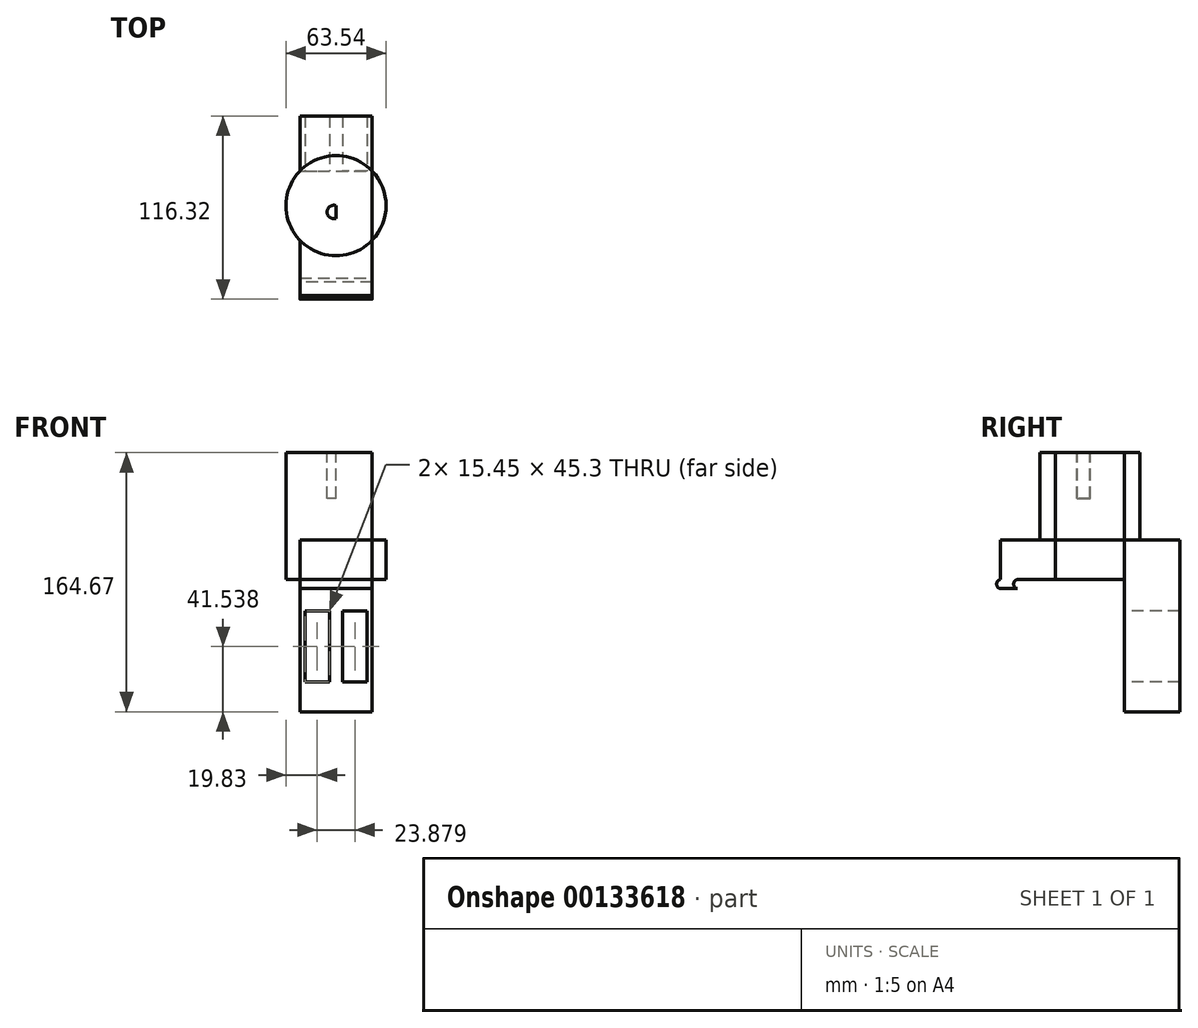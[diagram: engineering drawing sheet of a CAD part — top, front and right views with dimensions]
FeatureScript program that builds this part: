
annotation { "Feature Type Name" : "Feature", "Feature Type Description" : "" }
export const myFeature = defineFeature(function(context is Context, id is Id, definition is map)
    precondition{}
    {
        {
            var Q0;
            Q0=qCreatedBy(makeId("Top.planeOp"),FACE);
            var sketch = newSketch(context, id + "F0", { "sketchPlane" : qUnion([Q0])});
            skCircle(sketch, "E0", {"center": v(0, 0) * mm, "radius": 31.77 * mm});
            skLineSegment(sketch, "E1.bottom", {"start": v(22.97, -56.95) * mm, "end": v(-22.97, -56.95) * mm});
            skLineSegment(sketch, "E1.top", {"start": v(22.97, 56.95) * mm, "end": v(-22.97, 56.95) * mm});
            skLineSegment(sketch, "E1.left", {"start": v(22.97, -56.95) * mm, "end": v(22.97, 56.95) * mm});
            skLineSegment(sketch, "E1.right", {"start": v(-22.97, -56.95) * mm, "end": v(-22.97, 56.95) * mm});
            skSolve(sketch);
        }
        {
            var Q0;
            {var subQ0=sQuery(id+"F0.wireOp",EDGE,"E1.left");var subQ1=sQuery(id+"F0.wireOp",EDGE,"E0");var subQ2=makeQuery(id+"F0.imprint","INTERSECT",VERTEX,{"disambiguationData":[OD(0.0)],"derivedFrom":[subQ1,subQ0]});Q0=makeQuery(id+"F0.imprint","IMPRINT",FACE,{"disambiguationData":[TD([[makeQuery(id+"F0.imprint","IMPRINT",EDGE,{"disambiguationData":[TD([[subQ2,1.0]])],"derivedFrom":subQ1}),1.0]])]});}
            var Q1;
            {var subQ0=sQuery(id+"F0.wireOp",EDGE,"E1.right");var subQ1=sQuery(id+"F0.wireOp",EDGE,"E0");var subQ2=makeQuery(id+"F0.imprint","INTERSECT",VERTEX,{"disambiguationData":[OD(0.0)],"derivedFrom":[subQ1,subQ0]});Q1=makeQuery(id+"F0.imprint","IMPRINT",FACE,{"disambiguationData":[TD([[makeQuery(id+"F0.imprint","IMPRINT",EDGE,{"disambiguationData":[TD([[subQ2,1.0]])],"derivedFrom":subQ1}),1.0]])]});}
            var Q2;
            {var subQ0=sQuery(id+"F0.wireOp",EDGE,"E1.right");var subQ1=sQuery(id+"F0.wireOp",EDGE,"E0");var subQ2=makeQuery(id+"F0.imprint","INTERSECT",VERTEX,{"disambiguationData":[OD(0.0)],"derivedFrom":[subQ1,subQ0]});Q2=makeQuery(id+"F0.imprint","IMPRINT",FACE,{"disambiguationData":[TD([[makeQuery(id+"F0.imprint","IMPRINT",EDGE,{"disambiguationData":[TD([[subQ2,-1.0]])],"derivedFrom":subQ1}),1.0]])]});}
            extrude(context, id + "F1", {"entities" : qUnion([Q0, Q1, Q2]), "depth" : 80.54 * mm});
        }
        {
            var Q0;
            Q0=qSketchRegion(id+"F0",true);
            extrude(context, id + "F2", {"entities" : qUnion([Q0]), "operationType" : NewBodyOperationType.ADD, "depth" : 25 * mm});
        }
        {
            var Q0;
            {var subQ0=sQuery(id+"F0.wireOp",EDGE,"E0");Q0=makeQuery(id+"F2.boolean.opBoolean","MERGE",FACE,{"derivedFrom":[makeQuery(id+"F1.opExtrude","CAP_FACE",FACE,{"disambiguationData":[OSD([subQ0])],"isStart":true}),makeQuery(id+"F2.opExtrude","CAP_FACE",FACE,{"disambiguationData":[OSD([subQ0,sQuery(id+"F0.wireOp",EDGE,"E1.bottom"),sQuery(id+"F0.wireOp",EDGE,"E1.top"),sQuery(id+"F0.wireOp",EDGE,"E1.left"),sQuery(id+"F0.wireOp",EDGE,"E1.right")])],"isStart":true})]});}
            var sketch = newSketch(context, id + "F3", { "sketchPlane" : qUnion([Q0])});
            skLineSegment(sketch, "E2", {"start": v(-22.97, -21.95) * mm, "end": v(22.97, -21.95) * mm});
            skSolve(sketch);
        }
        {
            var Q0;
            Q0=makeQuery(id+"F3.imprint","IMPRINT",FACE,{"disambiguationData":[TD([[makeQuery(id+"F3.imprint","IMPRINT",EDGE,{"derivedFrom":sQuery(id+"F3.wireOp",EDGE,"E2")}),-1.0]])]});
            extrude(context, id + "F4", {"entities" : qUnion([Q0]), "operationType" : NewBodyOperationType.ADD, "depth" : 84.13 * mm});
        }
        {
            var Q0;
            Q0=makeQuery(id+"F4.opExtrude","SWEPT_FACE",FACE,{"disambiguationData":[OSD([sQuery(id+"F3.wireOp",EDGE,"E2")])]});
            var sketch = newSketch(context, id + "F5", { "sketchPlane" : qUnion([Q0])});
            skLineSegment(sketch, "E3", {"start": v(0, 0) * mm, "end": v(0, -84.13) * mm, "construction": true});
            skLineSegment(sketch, "E4.bottom", {"start": v(19.67, -65.24) * mm, "end": v(4.21, -65.24) * mm});
            skLineSegment(sketch, "E4.top", {"start": v(19.67, -19.94) * mm, "end": v(4.21, -19.94) * mm});
            skLineSegment(sketch, "E4.left", {"start": v(19.67, -65.24) * mm, "end": v(19.67, -19.94) * mm});
            skLineSegment(sketch, "E4.right", {"start": v(4.21, -65.24) * mm, "end": v(4.21, -19.94) * mm});
            skLineSegment(sketch, "E5.MirrorCS", {"start": v(-19.67, -19.94) * mm, "end": v(-4.21, -19.94) * mm});
            skLineSegment(sketch, "E6.MirrorCS", {"start": v(-19.67, -65.24) * mm, "end": v(-19.67, -19.94) * mm});
            skLineSegment(sketch, "E7.MirrorCS", {"start": v(-4.21, -65.24) * mm, "end": v(-4.21, -19.94) * mm});
            skLineSegment(sketch, "E8.MirrorCS", {"start": v(-19.67, -65.24) * mm, "end": v(-4.21, -65.24) * mm});
            skSolve(sketch);
        }
        {
            var Q0;
            Q0=makeQuery(id+"F5.imprint","IMPRINT",FACE,{"disambiguationData":[TD([[makeQuery(id+"F5.imprint","IMPRINT",EDGE,{"derivedFrom":sQuery(id+"F5.wireOp",EDGE,"E4.bottom")}),-1.0]])]});
            var Q1;
            Q1=makeQuery(id+"F5.imprint","IMPRINT",FACE,{"disambiguationData":[TD([[makeQuery(id+"F5.imprint","IMPRINT",EDGE,{"derivedFrom":sQuery(id+"F5.wireOp",EDGE,"E5.MirrorCS")}),-1.0]])]});
            extrude(context, id + "F6", {"entities" : qUnion([Q0, Q1]), "operationType" : NewBodyOperationType.REMOVE, "endBound" : BoundingType.THROUGH_ALL, "oppositeDirection" : true, "depth" : 25 * mm});
        }
        {
            var Q0;
            Q0=makeQuery(id+"F1.opExtrude","CAP_FACE",FACE,{"disambiguationData":[OSD([sQuery(id+"F0.wireOp",EDGE,"E0")])],"isStart":false});
            var sketch = newSketch(context, id + "F7", { "sketchPlane" : qUnion([Q0])});
            skArc(sketch, "E9", {"start": v(0, 0) * mm, "mid": v(-5.73, -4.04) * mm, "end": v(0, -8.08) * mm});
            skLineSegment(sketch, "E10", {"start": v(0, -8.08) * mm, "end": v(0, 0) * mm});
            skSolve(sketch);
        }
        {
            var Q0;
            Q0=qSketchRegion(id+"F7",true);
            extrude(context, id + "F8", {"entities" : qUnion([Q0]), "operationType" : NewBodyOperationType.REMOVE, "oppositeDirection" : true, "depth" : 29.17 * mm});
        }
        {
            var Q0;
            {var subQ0=sQuery(id+"F0.wireOp",EDGE,"E0");Q0=makeQuery(id+"F2.boolean.opBoolean","MERGE",FACE,{"derivedFrom":[makeQuery(id+"F1.opExtrude","CAP_FACE",FACE,{"disambiguationData":[OSD([subQ0])],"isStart":true}),makeQuery(id+"F2.opExtrude","CAP_FACE",FACE,{"disambiguationData":[OSD([subQ0,sQuery(id+"F0.wireOp",EDGE,"E1.bottom"),sQuery(id+"F0.wireOp",EDGE,"E1.top"),sQuery(id+"F0.wireOp",EDGE,"E1.left"),sQuery(id+"F0.wireOp",EDGE,"E1.right")])],"isStart":true})]});}
            var sketch = newSketch(context, id + "F9", { "sketchPlane" : qUnion([Q0])});
            skLineSegment(sketch, "E11", {"start": v(-22.97, 46.13) * mm, "end": v(22.97, 46.13) * mm});
            skSolve(sketch);
        }
        {
            var Q0;
            Q0=qCreatedBy(makeId("Right.planeOp"),FACE);
            var sketch = newSketch(context, id + "F10", { "sketchPlane" : qUnion([Q0])});
            skLineSegment(sketch, "E12.0.0", {"start": v(-56.95, 0) * mm, "end": v(-46.13, 0) * mm});
            skLineSegment(sketch, "E12.0.2", {"start": v(-46.13, 0) * mm, "end": v(-56.95, 0) * mm});
            skArc(sketch, "E13", {"start": v(-51.54, 0) * mm, "mid": v(-53.97, -2.94) * mm, "end": v(-51.54, -5.89) * mm});
            skPoint(sketch, "E13.endSnap0", {"position": v(-51.54, 0) * mm});
            skSolve(sketch);
        }
        {
            var Q0;
            {var subQ0=sQuery(id+"F9.wireOp",EDGE,"E11");Q0=makeQuery(id+"F9.imprint","IMPRINT",FACE,{"disambiguationData":[TD([[makeQuery(id+"F9.imprint","IMPRINT",EDGE,{"derivedFrom":subQ0}),1.0]])]});}
            var Q1;
            Q1=sQuery(id+"F10.wireOp",EDGE,"E13");
            sweep(context, id + "F11", {"operationType" : NewBodyOperationType.ADD, "profiles" : qUnion([Q0]), "path" : qUnion([Q1]), "keepProfileOrientation" : true});
        }
    });
